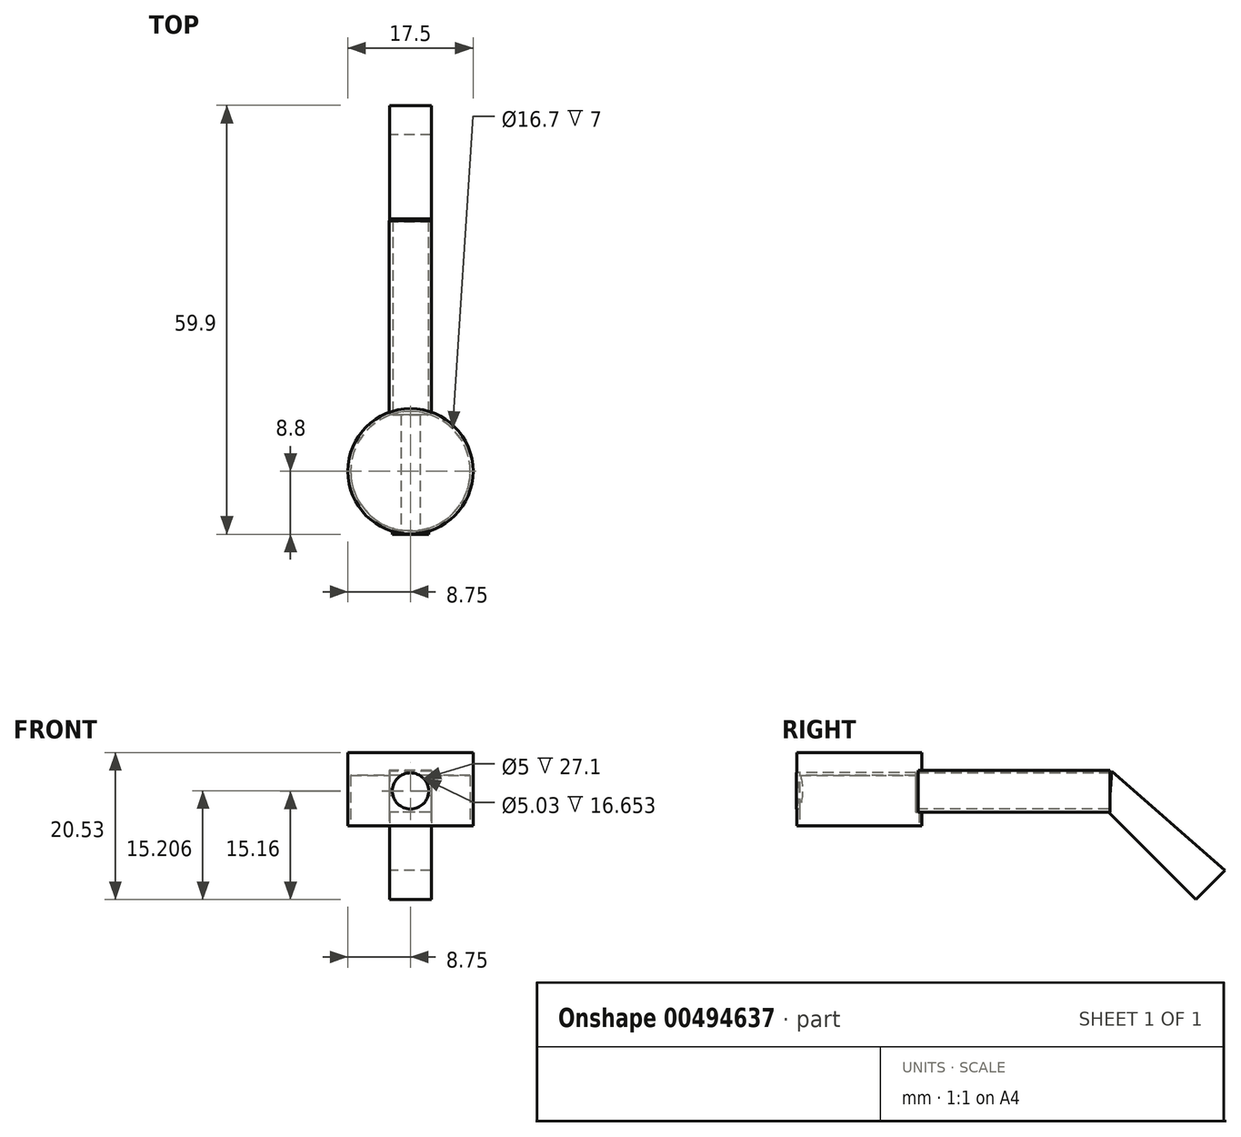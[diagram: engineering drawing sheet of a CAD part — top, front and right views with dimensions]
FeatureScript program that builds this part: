
annotation { "Feature Type Name" : "Feature", "Feature Type Description" : "" }
export const myFeature = defineFeature(function(context is Context, id is Id, definition is map)
    precondition{}
    {
        {
            var Q0;
            Q0=qCreatedBy(makeId("Top.planeOp"),FACE);
            var sketch = newSketch(context, id + "F0", { "sketchPlane" : qUnion([Q0])});
            skCircle(sketch, "E0", {"center": v(0, 0) * mm, "radius": 8.75 * mm});
            skSolve(sketch);
        }
        {
            var Q0;
            Q0=makeQuery(id+"F0.imprint","IMPRINT",FACE,{"disambiguationData":[TD([[makeQuery(id+"F0.imprint","IMPRINT",EDGE,{"derivedFrom":sQuery(id+"F0.wireOp",EDGE,"E0")}),1.0]])]});
            extrude(context, id + "F1", {"entities" : qUnion([Q0]), "depth" : 10.2 * mm});
        }
        {
            var Q0;
            Q0=qCreatedBy(makeId("Front.planeOp"),FACE);
            var sketch = newSketch(context, id + "F2", { "sketchPlane" : qUnion([Q0])});
            skCircle(sketch, "E1", {"center": v(0, 4.83) * mm, "radius": 2.5 * mm});
            skSolve(sketch);
        }
        {
            var Q0;
            Q0=qCreatedBy(makeId("Front.planeOp"),FACE);
            var sketch = newSketch(context, id + "F3", { "sketchPlane" : qUnion([Q0])});
            skCircle(sketch, "E2", {"center": v(0, 4.88) * mm, "radius": 2.52 * mm});
            skSolve(sketch);
        }
        {
            var Q0;
            Q0 = qSketchRegion(id + "F3", true);
            var Q1;
            Q1=sQuery(id+"F3.wireOp",EDGE,"E2");
            extrude(context, id + "F4", {"entities" : qUnion([Q0]), "operationType" : NewBodyOperationType.REMOVE, "surfaceEntities" : qUnion([Q1]), "endBound" : BoundingType.SYMMETRIC, "oppositeDirection" : true, "depth" : 18.8 * mm});
        }
        {
            var Q0;
            Q0=makeQuery(id+"F1.opExtrude","CAP_FACE",FACE,{"disambiguationData":[OSD([sQuery(id+"F0.wireOp",EDGE,"E0")])],"isStart":true});
            var sketch = newSketch(context, id + "F5", { "sketchPlane" : qUnion([Q0])});
            skCircle(sketch, "E3", {"center": v(0, 0) * mm, "radius": 8.35 * mm});
            skSolve(sketch);
        }
        {
            var Q0;
            Q0=makeQuery(id+"F5.imprint","IMPRINT",FACE,{"disambiguationData":[TD([[makeQuery(id+"F5.imprint","IMPRINT",EDGE,{"derivedFrom":sQuery(id+"F5.wireOp",EDGE,"E3")}),1.0]])]});
            var Q1;
            Q1=sQuery(id+"F5.wireOp",EDGE,"E3");
            extrude(context, id + "F6", {"entities" : qUnion([Q0]), "operationType" : NewBodyOperationType.REMOVE, "surfaceEntities" : qUnion([Q1]), "oppositeDirection" : true, "depth" : 7 * mm});
        }
        {
            var Q0;
            Q0=makeQuery(id+"F2.imprint","IMPRINT",FACE,{"disambiguationData":[TD([[makeQuery(id+"F2.imprint","IMPRINT",EDGE,{"derivedFrom":sQuery(id+"F2.wireOp",EDGE,"E1")}),1.0]])]});
            cPlane(context, id + "F7", {"entities" : qUnion([Q0]), "cplaneType" : CPlaneType.OFFSET, "offset" : 8.8 * mm, "width" : 150 * mm, "height" : 150 * mm});
        }
        {
            var Q0;
            Q0=qCreatedBy(id+"F7.planeOp",FACE);
            var sketch = newSketch(context, id + "F8", { "sketchPlane" : qUnion([Q0])});
            skCircle(sketch, "E4", {"center": v(0, 4.85) * mm, "radius": 2.54 * mm});
            skSolve(sketch);
        }
        {
            var Q0;
            Q0=makeQuery(id+"F8.imprint","IMPRINT",FACE,{"disambiguationData":[TD([[makeQuery(id+"F8.imprint","IMPRINT",EDGE,{"derivedFrom":sQuery(id+"F8.wireOp",EDGE,"E4")}),1.0]])]});
            var Q1;
            Q1=sQuery(id+"F8.wireOp",EDGE,"E4");
            extrude(context, id + "F9", {"entities" : qUnion([Q0]), "surfaceEntities" : qUnion([Q1]), "oppositeDirection" : true, "depth" : 0.5 * mm});
        }
        {
            var Q0;
            Q0=qCreatedBy(makeId("Front.planeOp"),FACE);
            var sketch = newSketch(context, id + "F10", { "sketchPlane" : qUnion([Q0])});
            skLineSegment(sketch, "E5.bottom", {"start": v(2.95, 7.74) * mm, "end": v(-2.95, 7.74) * mm});
            skLineSegment(sketch, "E5.top", {"start": v(2.95, 1.9) * mm, "end": v(-2.95, 1.9) * mm});
            skLineSegment(sketch, "E5.left", {"start": v(2.95, 7.74) * mm, "end": v(2.95, 1.9) * mm});
            skLineSegment(sketch, "E5.right", {"start": v(-2.95, 7.74) * mm, "end": v(-2.95, 1.9) * mm});
            skPoint(sketch, "E5.middle", {"position": v(0, 4.82) * mm});
            skSolve(sketch);
        }
        {
            var Q0;
            Q0=makeQuery(id+"F10.imprint","IMPRINT",FACE,{"disambiguationData":[TD([[makeQuery(id+"F10.imprint","IMPRINT",EDGE,{"derivedFrom":sQuery(id+"F10.wireOp",EDGE,"E5.bottom")}),1.0]])]});
            extrude(context, id + "F11", {"entities" : qUnion([Q0]), "operationType" : NewBodyOperationType.ADD, "oppositeDirection" : true, "depth" : 35 * mm});
        }
        {
            var Q0;
            Q0=makeQuery(id+"F2.imprint","IMPRINT",FACE,{"disambiguationData":[TD([[makeQuery(id+"F2.imprint","IMPRINT",EDGE,{"derivedFrom":sQuery(id+"F2.wireOp",EDGE,"E1")}),1.0]])]});
            extrude(context, id + "F12", {"entities" : qUnion([Q0]), "operationType" : NewBodyOperationType.REMOVE, "oppositeDirection" : true, "depth" : 35 * mm});
        }
        {
            var Q0;
            Q0=makeQuery(id+"F11.opExtrude","CAP_FACE",FACE,{"disambiguationData":[OSD([sQuery(id+"F10.wireOp",EDGE,"E5.bottom"),sQuery(id+"F10.wireOp",EDGE,"E5.top"),sQuery(id+"F10.wireOp",EDGE,"E5.left"),sQuery(id+"F10.wireOp",EDGE,"E5.right")])],"isStart":true});
            extrude(context, id + "F13", {"entities" : qUnion([Q0]), "operationType" : NewBodyOperationType.REMOVE, "oppositeDirection" : true, "depth" : 7.9 * mm});
        }
        {
            var Q0;
            Q0=qCreatedBy(makeId("Right.planeOp"),FACE);
            var sketch = newSketch(context, id + "F14", { "sketchPlane" : qUnion([Q0])});
            skLineSegment(sketch, "E6", {"start": v(34.81, 1.89) * mm, "end": v(47.03, -10.33) * mm});
            skLineSegment(sketch, "E7", {"start": v(47.03, -10.33) * mm, "end": v(51.1, -6.26) * mm});
            skLineSegment(sketch, "E8", {"start": v(51.1, -6.26) * mm, "end": v(35.27, 7.62) * mm});
            skLineSegment(sketch, "E9", {"start": v(35.27, 7.62) * mm, "end": v(34.81, 1.89) * mm});
            skSolve(sketch);
        }
        {
            var Q0;
            Q0=makeQuery(id+"F14.imprint","IMPRINT",FACE,{"disambiguationData":[TD([[makeQuery(id+"F14.imprint","IMPRINT",EDGE,{"derivedFrom":sQuery(id+"F14.wireOp",EDGE,"E6")}),1.0]])]});
            extrude(context, id + "F15", {"entities" : qUnion([Q0]), "operationType" : NewBodyOperationType.ADD, "endBound" : BoundingType.SYMMETRIC, "depth" : 5.8 * mm});
        }
        {
            var Q0;
            Q0=makeQuery(id+"F15.opExtrude","SWEPT_FACE",FACE,{"disambiguationData":[OSD([sQuery(id+"F14.wireOp",EDGE,"E7")])]});
            var sketch = newSketch(context, id + "F16", { "sketchPlane" : qUnion([Q0])});
            skPoint(sketch, "E10.center.orphan", {"position": v(0, -41.55) * mm});
            skPoint(sketch, "E11.centerSnap0", {"position": v(2.9, -28.83) * mm});
            skPoint(sketch, "E11.center.orphan", {"position": v(0, -28.83) * mm});
            skCircle(sketch, "E12", {"center": v(0, -28.83) * mm, "radius": 1.56 * mm});
            skSolve(sketch);
        }
        {
            var Q0;
            Q0=makeQuery(id+"F16.imprint","IMPRINT",FACE,{"disambiguationData":[TD([[makeQuery(id+"F16.imprint","IMPRINT",EDGE,{"derivedFrom":sQuery(id+"F16.wireOp",EDGE,"E12")}),1.0]])]});
            var Q1;
            Q1=sQuery(id+"F16.wireOp",EDGE,"E12");
            extrude(context, id + "F17", {"entities" : qUnion([Q0]), "operationType" : NewBodyOperationType.REMOVE, "surfaceEntities" : qUnion([Q1]), "oppositeDirection" : true, "depth" : 20.5 * mm});
        }
    });
